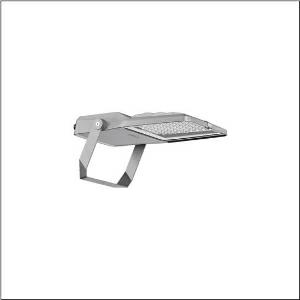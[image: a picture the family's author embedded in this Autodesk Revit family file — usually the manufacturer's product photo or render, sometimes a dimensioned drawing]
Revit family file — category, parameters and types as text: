
# Revit family: floodlight_fl_21_iq_mini___pl52_5xa7772b2d1a_4cc7
name_source: partatom
category: Lighting Fixtures
units: mm (PartAtom-declared; Revit-internal decimal feet)

## family parameters
Cut with Voids When Loaded = No
Host = Face
Light Source = No
Part Type = Normal
Room Calculation Point = No
Round Connector Dimension = Use Diameter
Shared = No

## types (1)
- --- (1 x LED, 6240 lm, 45.5 W, 3000K)
    Apparent Load = 46 VA
    CIE Flux Codes = 26 60 98 100 100
    Color Rendering = 70
    Color Temperature = 3000K
    Default Elevation = 1800 mm
    Description = Floodlight FL 21 iQ mini, floodlight, primary light control with lens, of PMMA, primary optical cover: protective disc, of toughened safety glass, transparent, light distribution: PL52, light emission: direct distribution, installation type: surface-mounted, LED, High Power LED, rated luminous flux: 6.240lm, luminous efficacy: 137lm/W, light colour: 730, colour temperature: 3000K, control gear: iQ Street-Remote/DALI, control: Street-Remote, Auto-Match, Temp-Guard, Night-Set, Smart-Wire, Desk-Remote (wireless, voltage-free reading and setting of iQ features in the workshop via application-optimized NFC function/RFID function), optimised constant luminous flux control (CLO 2.0), with terminal, 6-pole, mains connection: 220..240V, AC, 50/60Hz, start of lifetime: 46W, end of service life: 48W, reduction: 22W, luminaire housing, of diecast aluminium, powder-coated, Siteco® metallic grey (DB 702S), corrosivity category C5 mid according to DIN EN ISO 12944, suitable for swimming pools, chlorine-resistant, sealing non-destructively replaceable, mounting bracket, of steel, galvanised, powder-coated, Siteco® metallic grey (DB 702S), protection rating (complete): IP66, insulation class (complete): insulation class II (safety insulation), certification: CE, ENEC, VDE, protection symbol: D, impact resistance: IK08, permissible operating ambient temperature: -40..+40°C, permissible operating ambient temperature for outdoor applications: -40..+50°C, standard: DIN EN 12944, LABS conformity tested according to VDMA 24364:2018-05, packaging unit: 1 piece

Light Distribution: PL52
    Height = 70 mm
    Lamp = 1 x LED
    Lamp Light Flux = 6240 lm
    Lamp Power = 45.5 W
    Lamp count = 1
    Length = 485 mm
    Luminous efficacy = 137 lm/W
    Manufacturer = Siteco
    ModVariant = No
    Model = 5XA7772B2D1A
    Number of Poles = 1
    OnlyDefault = Yes
    Power Factor = 1
    Product Name = Floodlight FL 21 iQ mini | PL52
    Product group = floodlight | pylon annexe
    ProductGroupID = 6200
    Protection Class = Protection class II
    Protection Degree = IP 66
    RLX_Detail_Level = 1
    RLX_Emergency_Light_Flux = 0 lm
    RLX_Emergency_Type = 0
    RLX_Emergency_Type_DB = No
    RlxData = <blob elided: 96373 chars, md5=415f32da>
    Socket = socket
    Standby Power = 0 W
    System Light Flux = 6240 lm
    System Power = 46 W
    Type Comments = factory setting: luminous flux: 100 % | dim-lin: 254 | 463 mA
    Type Image = l_1006845.jpg
    URL = http://relux.com
    VarID = @adj_164916
    Voltage = 0 V
    Weight = 0.00 kg
    Width = 337 mm

## geometry (parser evidence)
native form markers: Blend x4, Sweep x14
no freeform markers — native parametric forms only
